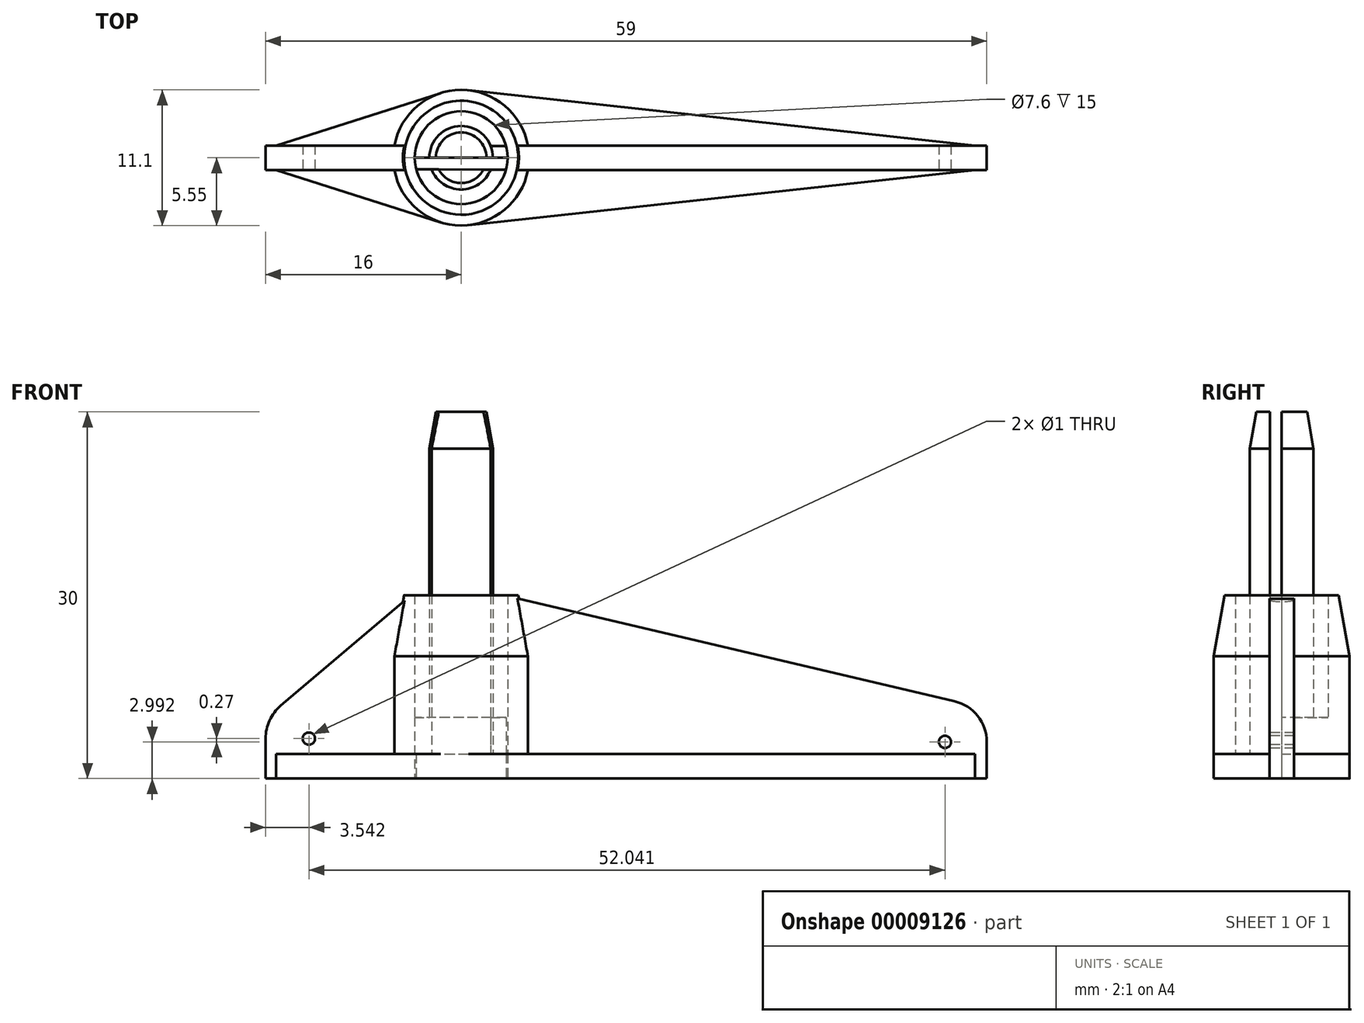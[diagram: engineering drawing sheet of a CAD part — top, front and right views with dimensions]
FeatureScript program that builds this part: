
annotation { "Feature Type Name" : "Feature", "Feature Type Description" : "" }
export const myFeature = defineFeature(function(context is Context, id is Id, definition is map)
    precondition{}
    {
        {
            var Q0;
            Q0=qCreatedBy(makeId("Top.planeOp"),FACE);
            var sketch = newSketch(context, id + "F0", { "sketchPlane" : qUnion([Q0])});
            skCircle(sketch, "E0", {"center": v(0, 0) * mm, "radius": 2.6 * mm});
            skCircle(sketch, "E1", {"center": v(0, 0) * mm, "radius": 3.8 * mm});
            skCircle(sketch, "E2", {"center": v(0, 0) * mm, "radius": 5.55 * mm});
            skArc(sketch, "E3", {"start": v(-15.3, 0.95) * mm, "mid": v(-16, 0) * mm, "end": v(-15.3, -0.95) * mm});
            skArc(sketch, "E4", {"start": v(42.1, -1) * mm, "mid": v(43, 0) * mm, "end": v(42.1, 1) * mm});
            skLineSegment(sketch, "E5", {"start": v(-15.3, 0.95) * mm, "end": v(-1.68, 5.29) * mm});
            skLineSegment(sketch, "E6", {"start": v(42.1, 1) * mm, "end": v(0.6, 5.52) * mm});
            skLineSegment(sketch, "E7", {"start": v(-4.9, 0) * mm, "end": v(7.85, 0) * mm});
            skLineSegment(sketch, "E8.0.MirrorCS", {"start": v(42.1, -1) * mm, "end": v(0.6, -5.52) * mm});
            skLineSegment(sketch, "E9.0.MirrorCS", {"start": v(-15.3, -0.95) * mm, "end": v(-1.68, -5.29) * mm});
            skLineSegment(sketch, "E10", {"start": v(-15.3, 0.95) * mm, "end": v(42.1, 1) * mm});
            skLineSegment(sketch, "E11", {"start": v(-15.3, -0.95) * mm, "end": v(42.1, -1) * mm});
            skLineSegment(sketch, "E12", {"start": v(-16, 0) * mm, "end": v(-7.54, 0) * mm});
            skLineSegment(sketch, "E13", {"start": v(43, 0) * mm, "end": v(21.08, 0) * mm});
            skSolve(sketch);
        }
        {
            var Q0;
            {var subQ0=sQuery(id+"F0.wireOp",EDGE,"E7");var subQ1=sQuery(id+"F0.wireOp",EDGE,"E0");var subQ2=makeQuery(id+"F0.imprint","INTERSECT",VERTEX,{"disambiguationData":[OD(1.0)],"derivedFrom":[subQ1,subQ0]});Q0=makeQuery(id+"F0.imprint","IMPRINT",FACE,{"disambiguationData":[TD([[makeQuery(id+"F0.imprint","IMPRINT",EDGE,{"disambiguationData":[TD([[subQ2,-1.0]])],"derivedFrom":subQ1}),1.0]])]});}
            var Q1;
            {var subQ0=sQuery(id+"F0.wireOp",EDGE,"E11");var subQ1=sQuery(id+"F0.wireOp",EDGE,"E0");var subQ3=makeQuery(id+"F0.imprint","INTERSECT",VERTEX,{"disambiguationData":[OD(0.0)],"derivedFrom":[subQ1,subQ0]});Q1=makeQuery(id+"F0.imprint","IMPRINT",FACE,{"disambiguationData":[TD([[makeQuery(id+"F0.imprint","IMPRINT",EDGE,{"disambiguationData":[TD([[subQ3,-1.0]])],"derivedFrom":subQ1}),1.0]])]});}
            var Q2;
            {var subQ0=sQuery(id+"F0.wireOp",EDGE,"E10");var subQ1=sQuery(id+"F0.wireOp",EDGE,"E0");var subQ3=makeQuery(id+"F0.imprint","INTERSECT",VERTEX,{"disambiguationData":[OD(0.0)],"derivedFrom":[subQ1,subQ0]});Q2=makeQuery(id+"F0.imprint","IMPRINT",FACE,{"disambiguationData":[TD([[makeQuery(id+"F0.imprint","IMPRINT",EDGE,{"disambiguationData":[TD([[subQ3,1.0]])],"derivedFrom":subQ1}),1.0]])]});}
            var Q3;
            {var subQ0=sQuery(id+"F0.wireOp",EDGE,"E10");var subQ1=sQuery(id+"F0.wireOp",EDGE,"E0");var subQ3=makeQuery(id+"F0.imprint","INTERSECT",VERTEX,{"disambiguationData":[OD(0.0)],"derivedFrom":[subQ1,subQ0]});Q3=makeQuery(id+"F0.imprint","IMPRINT",FACE,{"disambiguationData":[TD([[makeQuery(id+"F0.imprint","IMPRINT",EDGE,{"disambiguationData":[TD([[subQ3,-1.0]])],"derivedFrom":subQ1}),1.0]])]});}
            extrude(context, id + "F1", {"entities" : qUnion([Q0, Q1, Q2, Q3]), "depth" : 30 * mm});
        }
        {
            var Q0;
            {var subQ0=sQuery(id+"F0.wireOp",EDGE,"E10");var subQ1=sQuery(id+"F0.wireOp",EDGE,"E1");var subQ2=makeQuery(id+"F0.imprint","INTERSECT",VERTEX,{"disambiguationData":[OD(1.0)],"derivedFrom":[subQ1,subQ0]});Q0=makeQuery(id+"F0.imprint","IMPRINT",FACE,{"disambiguationData":[TD([[makeQuery(id+"F0.imprint","IMPRINT",EDGE,{"disambiguationData":[TD([[subQ2,-1.0]])],"derivedFrom":subQ1}),-1.0]])]});}
            var Q1;
            {var subQ1=sQuery(id+"F0.wireOp",EDGE,"E1");var subQ5=sQuery(id+"F0.wireOp",EDGE,"E7");var subQ6=makeQuery(id+"F0.imprint","INTERSECT",VERTEX,{"disambiguationData":[OD(1.0)],"derivedFrom":[subQ1,subQ5]});Q1=makeQuery(id+"F0.imprint","IMPRINT",FACE,{"disambiguationData":[TD([[makeQuery(id+"F0.imprint","IMPRINT",EDGE,{"disambiguationData":[TD([[subQ6,-1.0]])],"derivedFrom":subQ1}),-1.0]])]});}
            var Q2;
            {var subQ0=sQuery(id+"F0.wireOp",EDGE,"E11");var subQ1=sQuery(id+"F0.wireOp",EDGE,"E1");var subQ5=makeQuery(id+"F0.imprint","INTERSECT",VERTEX,{"disambiguationData":[OD(0.0)],"derivedFrom":[subQ1,subQ0]});Q2=makeQuery(id+"F0.imprint","IMPRINT",FACE,{"disambiguationData":[TD([[makeQuery(id+"F0.imprint","IMPRINT",EDGE,{"disambiguationData":[TD([[subQ5,-1.0]])],"derivedFrom":subQ1}),-1.0]])]});}
            var Q3;
            {var subQ0=sQuery(id+"F0.wireOp",EDGE,"E10");var subQ1=sQuery(id+"F0.wireOp",EDGE,"E1");var subQ2=makeQuery(id+"F0.imprint","INTERSECT",VERTEX,{"disambiguationData":[OD(0.0)],"derivedFrom":[subQ1,subQ0]});Q3=makeQuery(id+"F0.imprint","IMPRINT",FACE,{"disambiguationData":[TD([[makeQuery(id+"F0.imprint","IMPRINT",EDGE,{"disambiguationData":[TD([[subQ2,-1.0]])],"derivedFrom":subQ1}),-1.0]])]});}
            var Q4;
            {var subQ0=sQuery(id+"F0.wireOp",EDGE,"E10");var subQ1=sQuery(id+"F0.wireOp",EDGE,"E1");var subQ2=makeQuery(id+"F0.imprint","INTERSECT",VERTEX,{"disambiguationData":[OD(0.0)],"derivedFrom":[subQ1,subQ0]});Q4=makeQuery(id+"F0.imprint","IMPRINT",FACE,{"disambiguationData":[TD([[makeQuery(id+"F0.imprint","IMPRINT",EDGE,{"disambiguationData":[TD([[subQ2,1.0]])],"derivedFrom":subQ1}),-1.0]])]});}
            var Q5;
            {var subQ1=sQuery(id+"F0.wireOp",EDGE,"E1");var subQ5=sQuery(id+"F0.wireOp",EDGE,"E7");var subQ6=makeQuery(id+"F0.imprint","INTERSECT",VERTEX,{"disambiguationData":[OD(0.0)],"derivedFrom":[subQ1,subQ5]});Q5=makeQuery(id+"F0.imprint","IMPRINT",FACE,{"disambiguationData":[TD([[makeQuery(id+"F0.imprint","IMPRINT",EDGE,{"disambiguationData":[TD([[subQ6,1.0]])],"derivedFrom":subQ1}),-1.0]])]});}
            var Q6;
            {var subQ3=sQuery(id+"F0.wireOp",EDGE,"E1");var subQ5=sQuery(id+"F0.wireOp",EDGE,"E7");var subQ6=makeQuery(id+"F0.imprint","INTERSECT",VERTEX,{"disambiguationData":[OD(1.0)],"derivedFrom":[subQ3,subQ5]});Q6=makeQuery(id+"F0.imprint","IMPRINT",FACE,{"disambiguationData":[TD([[makeQuery(id+"F0.imprint","IMPRINT",EDGE,{"disambiguationData":[TD([[subQ6,1.0]])],"derivedFrom":subQ3}),-1.0]])]});}
            extrude(context, id + "F2", {"entities" : qUnion([Q0, Q1, Q2, Q3, Q4, Q5, Q6]), "depth" : 15 * mm});
        }
        {
            var Q0;
            Q0=qCreatedBy(makeId("Front.planeOp"),FACE);
            var sketch = newSketch(context, id + "F3", { "sketchPlane" : qUnion([Q0])});
            skLineSegment(sketch, "E14", {"start": v(-16, 0) * mm, "end": v(-16, 3.26) * mm});
            skLineSegment(sketch, "E15", {"start": v(43, 0) * mm, "end": v(43, 3) * mm});
            skArc(sketch, "E16", {"start": v(-14.75, 5.96) * mm, "mid": v(-15.67, 4.75) * mm, "end": v(-16, 3.26) * mm});
            skArc(sketch, "E17", {"start": v(43, 3) * mm, "mid": v(42.26, 5.11) * mm, "end": v(40.36, 6.32) * mm});
            skLineSegment(sketch, "E18", {"start": v(40.36, 6.32) * mm, "end": v(4.69, 14.7) * mm});
            skLineSegment(sketch, "E19", {"start": v(4.69, 14.7) * mm, "end": v(4.69, 0) * mm});
            skLineSegment(sketch, "E20", {"start": v(4.69, 0) * mm, "end": v(-4.58, 0) * mm});
            skLineSegment(sketch, "E21", {"start": v(-4.58, 0) * mm, "end": v(-4.58, 14.6) * mm});
            skLineSegment(sketch, "E22", {"start": v(-4.58, 14.6) * mm, "end": v(-14.75, 5.96) * mm});
            skLineSegment(sketch, "E23", {"start": v(-16, 0) * mm, "end": v(-4.58, 0) * mm});
            skLineSegment(sketch, "E24", {"start": v(43, 0) * mm, "end": v(4.69, 0) * mm});
            skCircle(sketch, "E25", {"center": v(-12.46, 3.26) * mm, "radius": 0.5 * mm});
            skCircle(sketch, "E26", {"center": v(39.58, 3) * mm, "radius": 0.5 * mm});
            skSolve(sketch);
        }
        {
            var Q0;
            Q0=makeQuery(id+"F3.imprint","IMPRINT",FACE,{"disambiguationData":[TD([[makeQuery(id+"F3.imprint","IMPRINT",EDGE,{"derivedFrom":sQuery(id+"F3.wireOp",EDGE,"E14")}),-1.0]])]});
            var Q1;
            Q1=makeQuery(id+"F3.imprint","IMPRINT",FACE,{"disambiguationData":[TD([[makeQuery(id+"F3.imprint","IMPRINT",EDGE,{"derivedFrom":sQuery(id+"F3.wireOp",EDGE,"E15")}),1.0]])]});
            extrude(context, id + "F4", {"entities" : qUnion([Q0, Q1]), "operationType" : NewBodyOperationType.ADD, "endBound" : BoundingType.SYMMETRIC, "oppositeDirection" : true, "depth" : 2 * mm});
        }
        {
            var Q0;
            Q0=makeQuery(id+"F2.opExtrude","CAP_EDGE",EDGE,{"disambiguationData":[OSD([sQuery(id+"F0.wireOp",EDGE,"E2")])],"isStart":false});
            chamfer(context, id + "F5", {"entities" : qUnion([Q0]), "chamferType" : ChamferType.OFFSET_ANGLE, "width" : 5 * mm, "oppositeDirection" : true, "angle" : 10 * degree, "tangentPropagation" : true});
        }
        {
            var Q0;
            Q0=makeQuery(id+"F1.opExtrude","CAP_EDGE",EDGE,{"disambiguationData":[OSD([sQuery(id+"F0.wireOp",EDGE,"E0")])],"isStart":false});
            chamfer(context, id + "F6", {"entities" : qUnion([Q0]), "chamferType" : ChamferType.OFFSET_ANGLE, "width" : 3 * mm, "oppositeDirection" : true, "angle" : 10 * degree, "tangentPropagation" : true});
        }
        {
            var Q0;
            {var subQ3=sQuery(id+"F0.wireOp",EDGE,"E5");Q0=makeQuery(id+"F0.imprint","IMPRINT",FACE,{"disambiguationData":[TD([[makeQuery(id+"F0.imprint","IMPRINT",EDGE,{"derivedFrom":subQ3}),-1.0]])]});}
            var Q1;
            {var subQ3=sQuery(id+"F0.wireOp",EDGE,"E3");Q1=makeQuery(id+"F0.imprint","IMPRINT",FACE,{"disambiguationData":[TD([[makeQuery(id+"F0.imprint","IMPRINT",EDGE,{"derivedFrom":subQ3}),1.0]])]});}
            var Q2;
            {var subQ3=sQuery(id+"F0.wireOp",EDGE,"E8.0.MirrorCS");Q2=makeQuery(id+"F0.imprint","IMPRINT",FACE,{"disambiguationData":[TD([[makeQuery(id+"F0.imprint","IMPRINT",EDGE,{"derivedFrom":subQ3}),-1.0]])]});}
            var Q3;
            {var subQ3=sQuery(id+"F0.wireOp",EDGE,"E4");Q3=makeQuery(id+"F0.imprint","IMPRINT",FACE,{"disambiguationData":[TD([[makeQuery(id+"F0.imprint","IMPRINT",EDGE,{"derivedFrom":subQ3}),1.0]])]});}
            var Q4;
            {var subQ3=sQuery(id+"F0.wireOp",EDGE,"E9.0.MirrorCS");Q4=makeQuery(id+"F0.imprint","IMPRINT",FACE,{"disambiguationData":[TD([[makeQuery(id+"F0.imprint","IMPRINT",EDGE,{"derivedFrom":subQ3}),1.0]])]});}
            var Q5;
            {var subQ3=sQuery(id+"F0.wireOp",EDGE,"E6");Q5=makeQuery(id+"F0.imprint","IMPRINT",FACE,{"disambiguationData":[TD([[makeQuery(id+"F0.imprint","IMPRINT",EDGE,{"derivedFrom":subQ3}),1.0]])]});}
            var Q6;
            {var subQ0=sQuery(id+"F0.wireOp",EDGE,"E10");var subQ3=sQuery(id+"F0.wireOp",EDGE,"E0");var subQ4=makeQuery(id+"F0.imprint","INTERSECT",VERTEX,{"disambiguationData":[OD(0.0)],"derivedFrom":[subQ3,subQ0]});Q6=makeQuery(id+"F0.imprint","IMPRINT",FACE,{"disambiguationData":[TD([[makeQuery(id+"F0.imprint","IMPRINT",EDGE,{"disambiguationData":[TD([[subQ4,-1.0]])],"derivedFrom":subQ3}),-1.0]])]});}
            var Q7;
            {var subQ0=sQuery(id+"F0.wireOp",EDGE,"E10");var subQ3=sQuery(id+"F0.wireOp",EDGE,"E0");var subQ4=makeQuery(id+"F0.imprint","INTERSECT",VERTEX,{"disambiguationData":[OD(1.0)],"derivedFrom":[subQ3,subQ0]});Q7=makeQuery(id+"F0.imprint","IMPRINT",FACE,{"disambiguationData":[TD([[makeQuery(id+"F0.imprint","IMPRINT",EDGE,{"disambiguationData":[TD([[subQ4,-1.0]])],"derivedFrom":subQ3}),-1.0]])]});}
            var Q8;
            {var subQ0=sQuery(id+"F0.wireOp",EDGE,"E10");var subQ3=sQuery(id+"F0.wireOp",EDGE,"E0");var subQ4=makeQuery(id+"F0.imprint","INTERSECT",VERTEX,{"disambiguationData":[OD(0.0)],"derivedFrom":[subQ3,subQ0]});Q8=makeQuery(id+"F0.imprint","IMPRINT",FACE,{"disambiguationData":[TD([[makeQuery(id+"F0.imprint","IMPRINT",EDGE,{"disambiguationData":[TD([[subQ4,1.0]])],"derivedFrom":subQ3}),-1.0]])]});}
            var Q9;
            {var subQ3=sQuery(id+"F0.wireOp",EDGE,"E0");var subQ5=sQuery(id+"F0.wireOp",EDGE,"E7");var subQ7=makeQuery(id+"F0.imprint","INTERSECT",VERTEX,{"disambiguationData":[OD(0.0)],"derivedFrom":[subQ3,subQ5]});Q9=makeQuery(id+"F0.imprint","IMPRINT",FACE,{"disambiguationData":[TD([[makeQuery(id+"F0.imprint","IMPRINT",EDGE,{"disambiguationData":[TD([[subQ7,1.0]])],"derivedFrom":subQ3}),-1.0]])]});}
            var Q10;
            {var subQ0=sQuery(id+"F0.wireOp",EDGE,"E11");var subQ3=sQuery(id+"F0.wireOp",EDGE,"E0");var subQ6=makeQuery(id+"F0.imprint","INTERSECT",VERTEX,{"disambiguationData":[OD(0.0)],"derivedFrom":[subQ3,subQ0]});Q10=makeQuery(id+"F0.imprint","IMPRINT",FACE,{"disambiguationData":[TD([[makeQuery(id+"F0.imprint","IMPRINT",EDGE,{"disambiguationData":[TD([[subQ6,-1.0]])],"derivedFrom":subQ3}),-1.0]])]});}
            var Q11;
            {var subQ3=sQuery(id+"F0.wireOp",EDGE,"E0");var subQ5=sQuery(id+"F0.wireOp",EDGE,"E7");var subQ7=makeQuery(id+"F0.imprint","INTERSECT",VERTEX,{"disambiguationData":[OD(1.0)],"derivedFrom":[subQ3,subQ5]});Q11=makeQuery(id+"F0.imprint","IMPRINT",FACE,{"disambiguationData":[TD([[makeQuery(id+"F0.imprint","IMPRINT",EDGE,{"disambiguationData":[TD([[subQ7,-1.0]])],"derivedFrom":subQ3}),-1.0]])]});}
            extrude(context, id + "F7", {"entities" : qUnion([Q0, Q1, Q2, Q3, Q4, Q5, Q6, Q7, Q8, Q9, Q10, Q11]), "operationType" : NewBodyOperationType.ADD, "depth" : 2 * mm});
        }
        {
            var Q0;
            {var subQ0=sQuery(id+"F0.wireOp",EDGE,"E7");var subQ3=sQuery(id+"F0.wireOp",EDGE,"E0");var subQ4=makeQuery(id+"F0.imprint","INTERSECT",VERTEX,{"disambiguationData":[OD(0.0)],"derivedFrom":[subQ3,subQ0]});Q0=makeQuery(id+"F0.imprint","IMPRINT",FACE,{"disambiguationData":[TD([[makeQuery(id+"F0.imprint","IMPRINT",EDGE,{"disambiguationData":[TD([[subQ4,1.0]])],"derivedFrom":subQ3}),-1.0]])]});}
            var Q1;
            {var subQ0=sQuery(id+"F0.wireOp",EDGE,"E10");var subQ3=sQuery(id+"F0.wireOp",EDGE,"E0");var subQ4=makeQuery(id+"F0.imprint","INTERSECT",VERTEX,{"disambiguationData":[OD(0.0)],"derivedFrom":[subQ3,subQ0]});Q1=makeQuery(id+"F0.imprint","IMPRINT",FACE,{"disambiguationData":[TD([[makeQuery(id+"F0.imprint","IMPRINT",EDGE,{"disambiguationData":[TD([[subQ4,1.0]])],"derivedFrom":subQ3}),-1.0]])]});}
            extrude(context, id + "F8", {"entities" : qUnion([Q0, Q1]), "operationType" : NewBodyOperationType.ADD, "depth" : 5 * mm});
        }
    });
